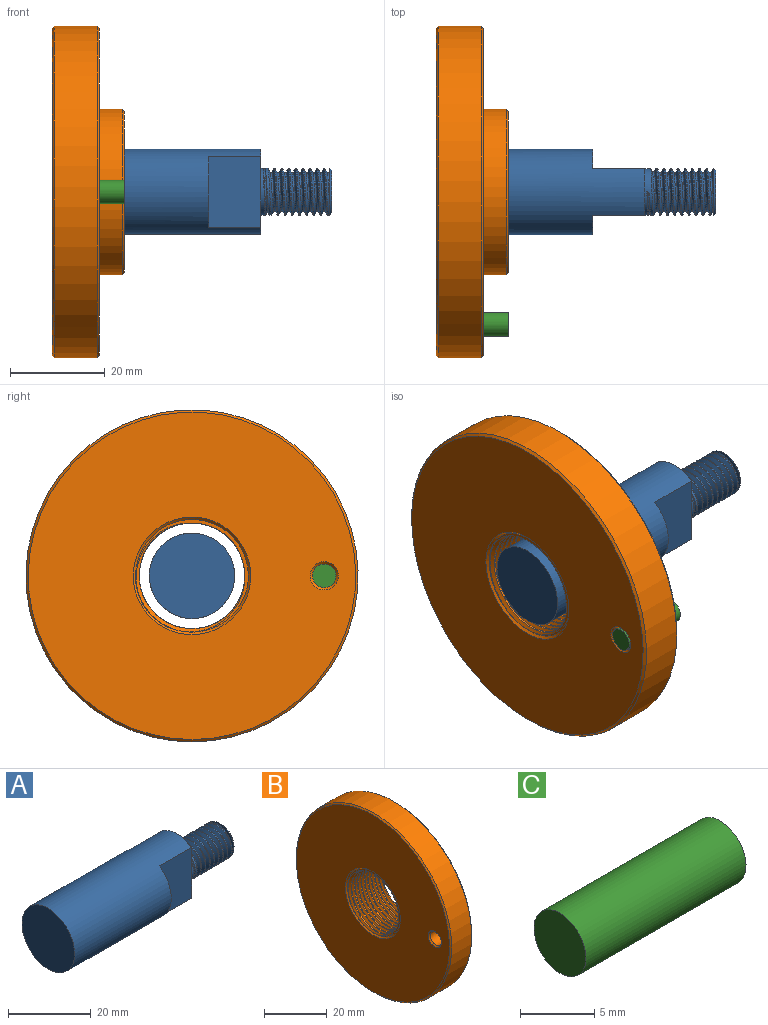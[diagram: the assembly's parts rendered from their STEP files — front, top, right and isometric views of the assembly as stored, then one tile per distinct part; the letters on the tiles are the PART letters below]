
ASSEMBLY  parts=3 mates=2
PART A: 27 faces, bbox 59.6x18.4x18.4 mm
  f0: plane 9.9x9mm, normal (1,0,0), area 45.9mm2, adj f2,f5,f6,f8
  f1: plane 15.03x4.05mm, normal (1,0,0), area 42.9mm2, adj f2,f6
  f2: cylinder r=9mm len=44mm, axis (-1,0,0), area 2096.7mm2, adj f0,f1,f3,f4,f5,f6,f7
  f3: plane 15.03x4.05mm, normal (1,0,0), area 42.9mm2, adj f2,f5
  f4: plane 18x18mm, normal (-1,0,0), area 254.5mm2, adj f2
  f5: plane 15.03x11mm, normal (0,-1,0), area 165.4mm2, adj f0,f2,f3,f7
  f6: plane 15.03x11mm, normal (0,1,0), area 165.4mm2, adj f0,f1,f2,f7
  f7: plane 9.9x9mm, normal (1,0,0), area 45.9mm2, adj f2,f5,f6,f8
  f8: cylinder r=4.95mm len=9.9mm, axis (-1,0,0), area 42.6mm2, adj f0,f7,f9,f19,f20,f21,f24
  f9: cylinder r=4.95mm len=9.9mm, axis (-1,0,0), area 5.8mm2, adj f8,f10,f23,f24
  f10: cylinder r=4.95mm len=9.9mm, axis (-1,0,0), area 5.8mm2, adj f9,f11,f23,f24
  f11: cylinder r=4.95mm len=9.9mm, axis (-1,0,0), area 5.8mm2, adj f10,f12,f23,f24
  f12: cylinder r=4.95mm len=9.9mm, axis (-1,0,0), area 5.8mm2, adj f11,f13,f23,f24
  f13: cylinder r=4.95mm len=9.9mm, axis (-1,0,0), area 5.8mm2, adj f12,f14,f23,f24
  f14: cylinder r=4.95mm len=9.9mm, axis (-1,0,0), area 5.8mm2, adj f13,f15,f23,f24
  f15: cylinder r=4.95mm len=9.9mm, axis (-1,0,0), area 5.8mm2, adj f14,f16,f23,f24
  f16: cylinder r=4.95mm len=9.9mm, axis (-1,0,0), area 4.2mm2, adj f15,f18,f23,f24
  f17: plane 8.9x8.9mm, normal (1,0,0), area 62.2mm2, adj f18
  f18: cone r=4.45mm half-angle=45deg, axis (-1,0,0), area 20.9mm2, adj f16,f17,f26
  f19: plane 0.46x0.15mm, normal (-0.01,-1,0), area 0mm2, adj f8,f20,f21,f25
  f20: bspline ~11.06x10.73mm, area 14.9mm2, adj f8,f19,f23,f25
  f21: bspline ~11.06x10.73mm, area 14.8mm2, adj f8,f19,f24,f25
  f22: bspline ~13.13x9.56mm, area 88.9mm2, adj f23,f24,f25,f26
  f23: bspline ~12.72x11.43mm, area 212.8mm2, adj f9,f10,f11,f12,f13,f14,f15,f16
  f24: bspline ~13.72x11.43mm, area 228.6mm2, adj f8,f9,f10,f11,f12,f13,f14,f15
  f25: bspline ~9.43x9.09mm, area 11.8mm2, adj f19,f20,f21,f22
  f26: plane 10.32x10.16mm, normal (-1,0,0), area 13.6mm2, adj f18,f22,f23,f24
PART B: 17 faces, bbox 16.5x70.5x70.5 mm
  f0: cylinder r=17.48mm len=34.95mm, axis (-1,0,0), area 521.5mm2, adj f5,f10
  f1: plane 34.47x34.47mm, normal (1,0,0), area 490.6mm2, adj f10,f11,f12,f13,f16
  f2: plane 69x69mm, normal (-1,0,0), area 3230.4mm2, adj f6,f7,f8
  f3: cylinder r=35mm len=70mm, axis (-1,0,0), area 1979.2mm2, adj f7,f9
  f4: cylinder r=2.48mm len=9.5mm, axis (-1,0,0), area 147.7mm2, adj f5,f6
  f5: plane 69x69mm, normal (1,0,0), area 2760.7mm2, adj f0,f4,f9
  f6: cone r=2.98mm half-angle=45deg, axis (-1,0,0), area 12.1mm2, adj f2,f4
  f7: cone r=35mm half-angle=45deg, axis (1,0,0), area 154.4mm2, adj f2,f3
  f8: cone r=12.38mm half-angle=45deg, axis (-1,0,0), area 53.9mm2, adj f2,f14,f15
  f9: cone r=34.5mm half-angle=45deg, axis (-1,0,0), area 154.4mm2, adj f3,f5
  f10: cone r=16.98mm half-angle=45deg, axis (-1,0,0), area 76.5mm2, adj f0,f1
  f11: bspline ~27.57x23.87mm, area 664mm2, adj f1,f13,f14,f15,f16
  f12: bspline ~27.57x23.87mm, area 669.7mm2, adj f1,f13,f14,f15,f16
  f13: bspline ~27.72x24.01mm, area 160.5mm2, adj f1,f11,f12,f14
  f14: plane 8.94x8.79mm, normal (1,0,0), area 1mm2, adj f8,f11,f12,f13
  f15: plane 24.22x24.22mm, normal (-1,0,0), area 29.4mm2, adj f8,f11,f12,f16
  f16: cylinder r=11.12mm len=22.25mm, axis (1,0,0), area 374.1mm2, adj f1,f11,f12,f15
PART C: 3 faces, bbox 15.3x5x5 mm
  f0: cylinder r=2.48mm len=15.25mm, axis (-1,0,0), area 237.2mm2, adj f1,f2
  f1: plane 4.95x4.95mm, normal (1,0,0), area 19.2mm2, adj f0
  f2: plane 4.95x4.95mm, normal (-1,0,0), area 19.2mm2, adj f0
PLACE A at identity
PLACE B at identity
PLACE C at identity
MATE fastened A.f2 <-> B.f8  axis (-1,0,0) through (0,0,0)mm
MATE fastened C.f0 <-> B.f4  axis (-1,0,0) through (0,-27.88,0)mm
